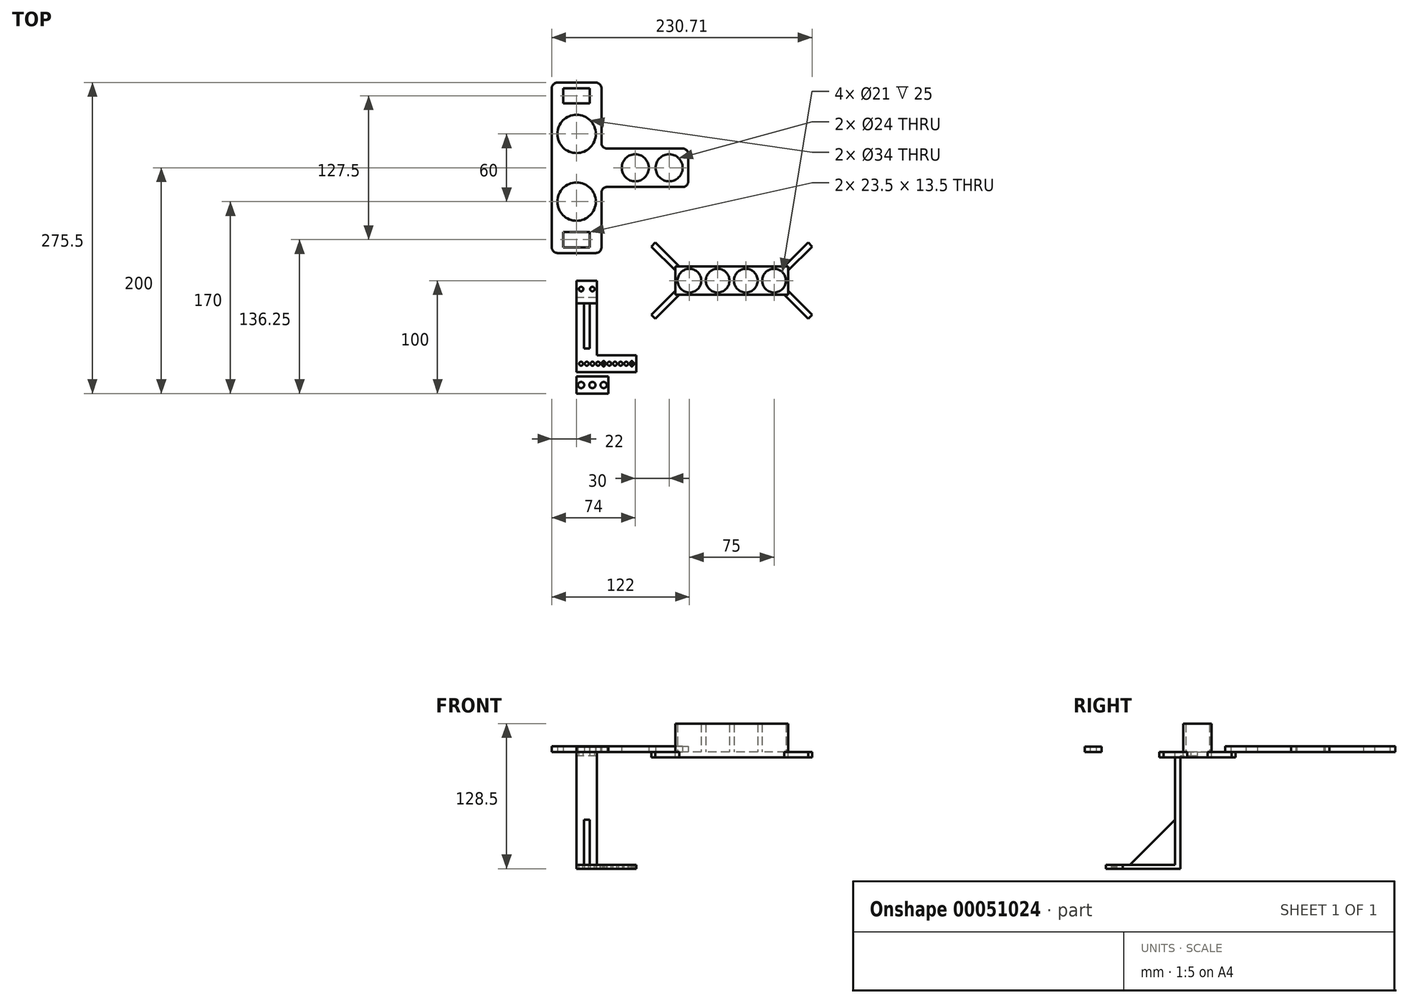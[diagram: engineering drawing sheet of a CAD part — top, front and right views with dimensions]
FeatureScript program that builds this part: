
annotation { "Feature Type Name" : "Feature", "Feature Type Description" : "" }
export const myFeature = defineFeature(function(context is Context, id is Id, definition is map)
    precondition{}
    {
        {
            var Q0;
            Q0=qCreatedBy(makeId("Top.planeOp"),FACE);
            var sketch = newSketch(context, id + "F0", { "sketchPlane" : qUnion([Q0])});
            skLineSegment(sketch, "E0", {"start": v(-42.25, 0) * mm, "end": v(184.17, 0) * mm, "construction": true});
            skCircle(sketch, "E1", {"center": v(0, 30) * mm, "radius": 17 * mm});
            skLineSegment(sketch, "E2.direction1", {"start": v(0, 30) * mm, "end": v(0, -25) * mm, "construction": true});
            skLineSegment(sketch, "E3", {"start": v(-80.48, 30) * mm, "end": v(147.23, 30) * mm, "construction": true});
            skCircle(sketch, "E4.MirrorC", {"center": v(0, -30) * mm, "radius": 17 * mm});
            skLineSegment(sketch, "E5.bottom", {"start": v(-11.75, 70.5) * mm, "end": v(11.75, 70.5) * mm});
            skLineSegment(sketch, "E5.top", {"start": v(-11.75, 57) * mm, "end": v(11.75, 57) * mm});
            skLineSegment(sketch, "E5.left", {"start": v(-11.75, 70.5) * mm, "end": v(-11.75, 57) * mm});
            skLineSegment(sketch, "E5.right", {"start": v(11.75, 70.5) * mm, "end": v(11.75, 57) * mm});
            skLineSegment(sketch, "E6.MirrorCS", {"start": v(-11.75, -57) * mm, "end": v(11.75, -57) * mm});
            skLineSegment(sketch, "E7.MirrorCS", {"start": v(-11.75, -70.5) * mm, "end": v(-11.75, -57) * mm});
            skLineSegment(sketch, "E8.MirrorCS", {"start": v(11.75, -70.5) * mm, "end": v(11.75, -57) * mm});
            skLineSegment(sketch, "E9.MirrorCS", {"start": v(-11.75, -70.5) * mm, "end": v(11.75, -70.5) * mm});
            skLineSegment(sketch, "E10", {"start": v(-22, 0) * mm, "end": v(-22, 75.5) * mm});
            skLineSegment(sketch, "E11", {"start": v(-22, 75.5) * mm, "end": v(22, 75.5) * mm});
            skLineSegment(sketch, "E12", {"start": v(22, 75.5) * mm, "end": v(22, 17) * mm});
            skLineSegment(sketch, "E13", {"start": v(22, 17) * mm, "end": v(99, 17) * mm});
            skLineSegment(sketch, "E14", {"start": v(99, 17) * mm, "end": v(99, 0) * mm});
            skLineSegment(sketch, "E15.MirrorCS", {"start": v(99, -17) * mm, "end": v(99, 0) * mm});
            skLineSegment(sketch, "E16.MirrorCS", {"start": v(22, -17) * mm, "end": v(99, -17) * mm});
            skLineSegment(sketch, "E17.MirrorCS", {"start": v(22, -75.5) * mm, "end": v(22, -17) * mm});
            skLineSegment(sketch, "E18.MirrorCS", {"start": v(-22, 0) * mm, "end": v(-22, -75.5) * mm});
            skLineSegment(sketch, "E19.MirrorCS", {"start": v(-22, -75.5) * mm, "end": v(22, -75.5) * mm});
            skCircle(sketch, "E20", {"center": v(82, 0) * mm, "radius": 12 * mm});
            skCircle(sketch, "E21", {"center": v(52, 0) * mm, "radius": 12 * mm});
            skSolve(sketch);
        }
        {
            var Q0;
            Q0 = qSketchRegion(id + "F0", true);
            extrude(context, id + "F1", {"entities" : qUnion([Q0]), "depth" : 5 * mm});
        }
        {
            var Q0;
            Q0=makeQuery(id+"F1.opExtrude","SWEPT_EDGE",EDGE,{"disambiguationData":[OSD([sQuery(id+"F0.wireOp",EDGE,"E12"),sQuery(id+"F0.wireOp",EDGE,"E13")])]});
            var Q1;
            Q1=makeQuery(id+"F1.opExtrude","SWEPT_EDGE",EDGE,{"disambiguationData":[OSD([sQuery(id+"F0.wireOp",EDGE,"E16.MirrorCS"),sQuery(id+"F0.wireOp",EDGE,"E17.MirrorCS")])]});
            var Q2;
            Q2=makeQuery(id+"F1.opExtrude","SWEPT_EDGE",EDGE,{"disambiguationData":[OSD([sQuery(id+"F0.wireOp",EDGE,"E15.MirrorCS"),sQuery(id+"F0.wireOp",EDGE,"E16.MirrorCS")])]});
            var Q3;
            Q3=makeQuery(id+"F1.opExtrude","SWEPT_EDGE",EDGE,{"disambiguationData":[OSD([sQuery(id+"F0.wireOp",EDGE,"E13"),sQuery(id+"F0.wireOp",EDGE,"E14")])]});
            var Q4;
            Q4=makeQuery(id+"F1.opExtrude","SWEPT_EDGE",EDGE,{"disambiguationData":[OSD([sQuery(id+"F0.wireOp",EDGE,"E11"),sQuery(id+"F0.wireOp",EDGE,"E12")])]});
            var Q5;
            Q5=makeQuery(id+"F1.opExtrude","SWEPT_EDGE",EDGE,{"disambiguationData":[OSD([sQuery(id+"F0.wireOp",EDGE,"E10"),sQuery(id+"F0.wireOp",EDGE,"E11")])]});
            var Q6;
            Q6=makeQuery(id+"F1.opExtrude","SWEPT_EDGE",EDGE,{"disambiguationData":[OSD([sQuery(id+"F0.wireOp",EDGE,"E18.MirrorCS"),sQuery(id+"F0.wireOp",EDGE,"E19.MirrorCS")])]});
            var Q7;
            Q7=makeQuery(id+"F1.opExtrude","SWEPT_EDGE",EDGE,{"disambiguationData":[OSD([sQuery(id+"F0.wireOp",EDGE,"E17.MirrorCS"),sQuery(id+"F0.wireOp",EDGE,"E19.MirrorCS")])]});
            fillet(context, id + "F2", {"entities" : qUnion([Q0, Q1, Q2, Q3, Q4, Q5, Q6, Q7]), "radius" : 5 * mm, "tangentPropagation" : true, "allowEdgeOverflow" : false});
        }
        {
            var Q0;
            Q0=makeQuery(id+"F1.opExtrude","SWEPT_BODY",BODY,{"disambiguationData":[OSD([sQuery(id+"F0.wireOp",EDGE,"E1"),sQuery(id+"F0.wireOp",EDGE,"7cc51740-4756-41ca-b782-dbcf211370ed"),sQuery(id+"F0.wireOp",EDGE,"5a0141ee-e843-40b7-996c-c0bd889232490.MirrorC"),sQuery(id+"F0.wireOp",EDGE,"E4.MirrorC"),sQuery(id+"F0.wireOp",EDGE,"E5.bottom"),sQuery(id+"F0.wireOp",EDGE,"E5.top"),sQuery(id+"F0.wireOp",EDGE,"E5.left"),sQuery(id+"F0.wireOp",EDGE,"E5.right"),sQuery(id+"F0.wireOp",EDGE,"E6.MirrorCS"),sQuery(id+"F0.wireOp",EDGE,"E7.MirrorCS"),sQuery(id+"F0.wireOp",EDGE,"E8.MirrorCS"),sQuery(id+"F0.wireOp",EDGE,"E9.MirrorCS"),sQuery(id+"F0.wireOp",EDGE,"E10"),sQuery(id+"F0.wireOp",EDGE,"E11"),sQuery(id+"F0.wireOp",EDGE,"E12"),sQuery(id+"F0.wireOp",EDGE,"E13"),sQuery(id+"F0.wireOp",EDGE,"E14"),sQuery(id+"F0.wireOp",EDGE,"E15.MirrorCS"),sQuery(id+"F0.wireOp",EDGE,"E16.MirrorCS"),sQuery(id+"F0.wireOp",EDGE,"E17.MirrorCS"),sQuery(id+"F0.wireOp",EDGE,"E18.MirrorCS"),sQuery(id+"F0.wireOp",EDGE,"E19.MirrorCS")])]});
            transform(context, id + "F3", {"entities" : qUnion([Q0]), "transformType" : TransformType.TRANSLATION_3D, "dx" : 0 * mm, "dy" : 200 * mm, "dz" : 0 * mm, "makeCopy" : false});
        }
        {
            var Q0;
            Q0=qCreatedBy(makeId("Right.planeOp"),FACE);
            var sketch = newSketch(context, id + "F4", { "sketchPlane" : qUnion([Q0])});
            skLineSegment(sketch, "E22.bottom", {"start": v(-15, -3.5) * mm, "end": v(0, -3.5) * mm});
            skLineSegment(sketch, "E22.top", {"start": v(-20, 0) * mm, "end": v(0, 0) * mm});
            skLineSegment(sketch, "E22.left", {"start": v(-20, 0) * mm, "end": v(-20, -3.5) * mm});
            skLineSegment(sketch, "E22.right", {"start": v(0, 0) * mm, "end": v(0, -3.5) * mm});
            skLineSegment(sketch, "E23.top", {"start": v(-20, -103.5) * mm, "end": v(-15, -103.5) * mm});
            skLineSegment(sketch, "E23.left", {"start": v(-20, -3.5) * mm, "end": v(-20, -100) * mm});
            skLineSegment(sketch, "E23.right", {"start": v(-15, -3.5) * mm, "end": v(-15, -103.5) * mm});
            skLineSegment(sketch, "E24.bottom", {"start": v(-15, -103.5) * mm, "end": v(-81.1, -103.5) * mm});
            skLineSegment(sketch, "E24.top", {"start": v(-20, -100) * mm, "end": v(-81.1, -100) * mm});
            skLineSegment(sketch, "E24.left", {"start": v(-15, -103.5) * mm, "end": v(-15, -100) * mm});
            skLineSegment(sketch, "E24.right", {"start": v(-81.1, -103.5) * mm, "end": v(-81.1, -100) * mm});
            skLineSegment(sketch, "E25", {"start": v(-73.6, -42.3) * mm, "end": v(-73.6, -123.52) * mm, "construction": true});
            skLineSegment(sketch, "E26", {"start": v(-7.5, 36.53) * mm, "end": v(-7.5, -125.68) * mm, "construction": true});
            skSolve(sketch);
        }
        {
            var Q0;
            Q0 = qSketchRegion(id + "F4", true);
            extrude(context, id + "F5", {"entities" : qUnion([Q0]), "depth" : 53 * mm});
        }
        {
            var Q0;
            Q0=makeQuery(id+"F5.opExtrude","SWEPT_FACE",FACE,{"disambiguationData":[OSD([sQuery(id+"F4.wireOp",EDGE,"E22.top")])]});
            var sketch = newSketch(context, id + "F6", { "sketchPlane" : qUnion([Q0])});
            skCircle(sketch, "E27", {"center": v(4, -7.5) * mm, "radius": 2 * mm});
            skLineSegment(sketch, "E28", {"start": v(-26.36, -7.5) * mm, "end": v(67.35, -7.5) * mm, "construction": true});
            skCircle(sketch, "E29.1.0.0", {"center": v(14, -7.5) * mm, "radius": 2 * mm});
            skLineSegment(sketch, "E29.direction1", {"start": v(4, -7.5) * mm, "end": v(14, -7.5) * mm, "construction": true});
            skSolve(sketch);
        }
        {
            var Q0;
            Q0 = qSketchRegion(id + "F6", true);
            var Q1;
            Q1=makeQuery(id+"F5.opExtrude","SWEPT_FACE",FACE,{"disambiguationData":[OSD([sQuery(id+"F4.wireOp",EDGE,"E22.bottom")])]});
            extrude(context, id + "F7", {"entities" : qUnion([Q0]), "operationType" : NewBodyOperationType.REMOVE, "endBound" : BoundingType.UP_TO_SURFACE, "oppositeDirection" : true, "endBoundEntityFace" : qUnion([Q1]), "depth" : 25 * mm});
        }
        {
            var Q0;
            Q0=makeQuery(id+"F5.opExtrude","SWEPT_FACE",FACE,{"disambiguationData":[OSD([sQuery(id+"F4.wireOp",EDGE,"E22.top")])]});
            var sketch = newSketch(context, id + "F8", { "sketchPlane" : qUnion([Q0])});
            skLineSegment(sketch, "E30.bottom", {"start": v(53, 0) * mm, "end": v(18, 0) * mm});
            skLineSegment(sketch, "E30.top", {"start": v(53, -66.1) * mm, "end": v(18, -66.1) * mm});
            skLineSegment(sketch, "E30.left", {"start": v(53, 0) * mm, "end": v(53, -66.1) * mm});
            skLineSegment(sketch, "E30.right", {"start": v(18, 0) * mm, "end": v(18, -66.1) * mm});
            skSolve(sketch);
        }
        {
            var Q0;
            Q0 = qSketchRegion(id + "F8", true);
            extrude(context, id + "F9", {"entities" : qUnion([Q0]), "operationType" : NewBodyOperationType.REMOVE, "endBound" : BoundingType.THROUGH_ALL, "oppositeDirection" : true, "depth" : 25 * mm});
        }
        {
            var Q0;
            Q0=makeQuery(id+"F5.opExtrude","SWEPT_FACE",FACE,{"disambiguationData":[OSD([sQuery(id+"F4.wireOp",EDGE,"E24.top")])]});
            var sketch = newSketch(context, id + "F10", { "sketchPlane" : qUnion([Q0])});
            skLineSegment(sketch, "E31", {"start": v(-30.18, -73.6) * mm, "end": v(42.32, -73.6) * mm, "construction": true});
            skCircle(sketch, "E32", {"center": v(4, -73.6) * mm, "radius": 1.75 * mm});
            skCircle(sketch, "E33.1.0.0", {"center": v(9, -73.6) * mm, "radius": 1.75 * mm});
            skCircle(sketch, "E33.2.0.0", {"center": v(14, -73.6) * mm, "radius": 1.75 * mm});
            skLineSegment(sketch, "E33.direction1", {"start": v(4, -73.6) * mm, "end": v(9, -73.6) * mm, "construction": true});
            skCircle(sketch, "E34", {"center": v(24, -75.1) * mm, "radius": 0.9 * mm});
            skCircle(sketch, "E35", {"center": v(24, -73.6) * mm, "radius": 1.5 * mm, "construction": true});
            skCircle(sketch, "E36.1.0", {"center": v(25.5, -73.6) * mm, "radius": 0.9 * mm});
            skLineSegment(sketch, "E36.1.1", {"start": v(24, -127.78) * mm, "end": v(24, -55.28) * mm, "construction": true});
            skCircle(sketch, "E36.2.0", {"center": v(24, -72.1) * mm, "radius": 0.9 * mm});
            skLineSegment(sketch, "E36.2.1", {"start": v(78.18, -73.6) * mm, "end": v(5.68, -73.6) * mm, "construction": true});
            skCircle(sketch, "E36.3.0", {"center": v(22.5, -73.6) * mm, "radius": 0.9 * mm});
            skLineSegment(sketch, "E36.3.1", {"start": v(24, -19.42) * mm, "end": v(24, -91.92) * mm, "construction": true});
            skCircle(sketch, "E37.0.3.0", {"center": v(19, -73.6) * mm, "radius": 1.75 * mm});
            skPoint(sketch, "E38.1.0.0", {"position": v(49, -73.6) * mm});
            skCircle(sketch, "E38.1.0.1", {"center": v(39, -73.6) * mm, "radius": 1.75 * mm});
            skCircle(sketch, "E38.1.0.2", {"center": v(34, -73.6) * mm, "radius": 1.75 * mm});
            skCircle(sketch, "E38.1.0.3", {"center": v(29, -73.6) * mm, "radius": 1.75 * mm});
            skCircle(sketch, "E38.1.0.4", {"center": v(44, -73.6) * mm, "radius": 1.75 * mm});
            skCircle(sketch, "E38.1.0.5", {"center": v(47.5, -73.6) * mm, "radius": 0.9 * mm});
            skCircle(sketch, "E38.1.0.6", {"center": v(49, -72.1) * mm, "radius": 0.9 * mm});
            skCircle(sketch, "E38.1.0.7", {"center": v(50.5, -73.6) * mm, "radius": 0.9 * mm});
            skCircle(sketch, "E38.1.0.8", {"center": v(49, -73.6) * mm, "radius": 1.5 * mm, "construction": true});
            skCircle(sketch, "E38.1.0.9", {"center": v(49, -75.1) * mm, "radius": 0.9 * mm});
            skLineSegment(sketch, "E38.1.0.10", {"start": v(29, -73.6) * mm, "end": v(34, -73.6) * mm, "construction": true});
            skLineSegment(sketch, "E38.direction1", {"start": v(24, -73.6) * mm, "end": v(49, -73.6) * mm, "construction": true});
            skSolve(sketch);
        }
        {
            var Q0;
            Q0 = qSketchRegion(id + "F10", true);
            extrude(context, id + "F11", {"entities" : qUnion([Q0]), "operationType" : NewBodyOperationType.REMOVE, "endBound" : BoundingType.UP_TO_NEXT, "oppositeDirection" : true, "depth" : 25 * mm});
        }
        {
            var Q0;
            Q0=qCreatedBy(makeId("Right.planeOp"),FACE);
            cPlane(context, id + "F12", {"entities" : qUnion([Q0]), "cplaneType" : CPlaneType.OFFSET, "offset" : 9 * mm, "width" : 150 * mm, "height" : 150 * mm});
        }
        {
            var Q0;
            Q0=qCreatedBy(id+"F12.planeOp",FACE);
            var sketch = newSketch(context, id + "F13", { "sketchPlane" : qUnion([Q0])});
            skLineSegment(sketch, "E39", {"start": v(-20, -100) * mm, "end": v(-60, -100) * mm});
            skLineSegment(sketch, "E40", {"start": v(-60, -100) * mm, "end": v(-20, -60) * mm});
            skLineSegment(sketch, "E41", {"start": v(-20, -60) * mm, "end": v(-20, -100) * mm});
            skSolve(sketch);
        }
        {
            var Q0;
            Q0 = qSketchRegion(id + "F13", true);
            extrude(context, id + "F14", {"entities" : qUnion([Q0]), "operationType" : NewBodyOperationType.ADD, "endBound" : BoundingType.SYMMETRIC, "depth" : 5 * mm, "hasSecondDirection" : true, "secondDirectionOppositeDirection" : true, "secondDirectionDepth" : 2.5 * mm});
        }
        {
            var Q0;
            Q0=makeQuery(id+"F5.opExtrude","SWEPT_BODY",BODY,{"disambiguationData":[OSD([sQuery(id+"F4.wireOp",EDGE,"E22.bottom"),sQuery(id+"F4.wireOp",EDGE,"E22.top"),sQuery(id+"F4.wireOp",EDGE,"E22.left"),sQuery(id+"F4.wireOp",EDGE,"E22.right"),sQuery(id+"F4.wireOp",EDGE,"E23.left"),sQuery(id+"F4.wireOp",EDGE,"E23.right"),sQuery(id+"F4.wireOp",EDGE,"E24.bottom"),sQuery(id+"F4.wireOp",EDGE,"E24.top"),sQuery(id+"F4.wireOp",EDGE,"E24.left"),sQuery(id+"F4.wireOp",EDGE,"E24.right")])]});
            transform(context, id + "F15", {"entities" : qUnion([Q0]), "transformType" : TransformType.TRANSLATION_3D, "dx" : 0 * mm, "dy" : 100 * mm, "dz" : 0 * mm, "makeCopy" : false});
        }
        {
            var Q0;
            Q0=qCreatedBy(makeId("Top.planeOp"),FACE);
            var sketch = newSketch(context, id + "F16", { "sketchPlane" : qUnion([Q0])});
            skCircle(sketch, "E42", {"center": v(0, 0) * mm, "radius": 10.5 * mm});
            skCircle(sketch, "E43.1.0.0", {"center": v(25, 0) * mm, "radius": 10.5 * mm});
            skCircle(sketch, "E43.2.0.0", {"center": v(50, 0) * mm, "radius": 10.5 * mm});
            skCircle(sketch, "E43.3.0.0", {"center": v(75, 0) * mm, "radius": 10.5 * mm});
            skLineSegment(sketch, "E43.direction1", {"start": v(0, 0) * mm, "end": v(25, 0) * mm, "construction": true});
            skLineSegment(sketch, "E44.bottom", {"start": v(-12.5, 12.5) * mm, "end": v(87.5, 12.5) * mm});
            skLineSegment(sketch, "E44.top", {"start": v(-12.5, -12.5) * mm, "end": v(87.5, -12.5) * mm});
            skLineSegment(sketch, "E44.left", {"start": v(-12.5, 12.5) * mm, "end": v(-12.5, -12.5) * mm});
            skLineSegment(sketch, "E44.right", {"start": v(87.5, 12.5) * mm, "end": v(87.5, -12.5) * mm});
            skSolve(sketch);
        }
        {
            var Q0;
            Q0 = qSketchRegion(id + "F16", true);
            extrude(context, id + "F17", {"entities" : qUnion([Q0]), "depth" : 25 * mm});
        }
        {
            var Q0;
            Q0=makeQuery(id+"F17.opExtrude","CAP_FACE",FACE,{"disambiguationData":[OSD([sQuery(id+"F16.wireOp",EDGE,"E42"),sQuery(id+"F16.wireOp",EDGE,"E43.1.0.0"),sQuery(id+"F16.wireOp",EDGE,"E43.2.0.0"),sQuery(id+"F16.wireOp",EDGE,"E43.3.0.0"),sQuery(id+"F16.wireOp",EDGE,"E44.bottom"),sQuery(id+"F16.wireOp",EDGE,"E44.top"),sQuery(id+"F16.wireOp",EDGE,"E44.left"),sQuery(id+"F16.wireOp",EDGE,"E44.right")])],"isStart":true});
            var sketch = newSketch(context, id + "F18", { "sketchPlane" : qUnion([Q0])});
            skLineSegment(sketch, "E45", {"start": v(-12.5, 0) * mm, "end": v(-12.5, 8.96) * mm});
            skLineSegment(sketch, "E46", {"start": v(-8.96, 12.5) * mm, "end": v(37.5, 12.5) * mm});
            skLineSegment(sketch, "E47", {"start": v(37.5, 41.65) * mm, "end": v(37.5, -31.11) * mm, "construction": true});
            skLineSegment(sketch, "E48", {"start": v(-48.83, 0) * mm, "end": v(106.74, 0) * mm, "construction": true});
            skLineSegment(sketch, "E49", {"start": v(-12.5, 8.96) * mm, "end": v(-33.71, 30.18) * mm});
            skLineSegment(sketch, "E50", {"start": v(-33.71, 30.18) * mm, "end": v(-30.18, 33.71) * mm});
            skLineSegment(sketch, "E51", {"start": v(-30.18, 33.71) * mm, "end": v(-8.96, 12.5) * mm});
            skLineSegment(sketch, "E52", {"start": v(0, 0) * mm, "end": v(-44.63, 44.63) * mm, "construction": true});
            skLineSegment(sketch, "E53", {"start": v(-27.38, -5.91) * mm, "end": v(-4.16, 17.3) * mm, "construction": true});
            skLineSegment(sketch, "E54.MirrorCS", {"start": v(108.71, 30.18) * mm, "end": v(105.18, 33.71) * mm});
            skLineSegment(sketch, "E55.MirrorCS", {"start": v(105.18, 33.71) * mm, "end": v(83.96, 12.5) * mm});
            skLineSegment(sketch, "E56.MirrorCS", {"start": v(87.5, 8.96) * mm, "end": v(108.71, 30.18) * mm});
            skLineSegment(sketch, "E57.MirrorCS", {"start": v(87.5, 0) * mm, "end": v(87.5, 8.96) * mm});
            skLineSegment(sketch, "E58.MirrorCS", {"start": v(83.96, 12.5) * mm, "end": v(37.5, 12.5) * mm});
            skLineSegment(sketch, "E59.MirrorCS", {"start": v(-33.71, -30.18) * mm, "end": v(-30.18, -33.71) * mm});
            skLineSegment(sketch, "E60.MirrorCS", {"start": v(87.5, 0) * mm, "end": v(87.5, -8.96) * mm});
            skLineSegment(sketch, "E61.MirrorCS", {"start": v(87.5, -8.96) * mm, "end": v(108.71, -30.18) * mm});
            skLineSegment(sketch, "E62.MirrorCS", {"start": v(105.18, -33.71) * mm, "end": v(83.96, -12.5) * mm});
            skLineSegment(sketch, "E63.MirrorCS", {"start": v(108.71, -30.18) * mm, "end": v(105.18, -33.71) * mm});
            skLineSegment(sketch, "E64.MirrorCS", {"start": v(83.96, -12.5) * mm, "end": v(37.5, -12.5) * mm});
            skLineSegment(sketch, "E65.MirrorCS", {"start": v(-12.5, 0) * mm, "end": v(-12.5, -8.96) * mm});
            skLineSegment(sketch, "E66.MirrorCS", {"start": v(-8.96, -12.5) * mm, "end": v(37.5, -12.5) * mm});
            skLineSegment(sketch, "E67.MirrorCS", {"start": v(-30.18, -33.71) * mm, "end": v(-8.96, -12.5) * mm});
            skLineSegment(sketch, "E68.MirrorCS", {"start": v(-12.5, -8.96) * mm, "end": v(-33.71, -30.18) * mm});
            skSolve(sketch);
        }
        {
            var Q0;
            Q0 = qSketchRegion(id + "F18", true);
            extrude(context, id + "F19", {"entities" : qUnion([Q0]), "operationType" : NewBodyOperationType.ADD, "depth" : 5 * mm});
        }
        {
            var Q0;
            Q0=makeQuery(id+"F17.opExtrude","SWEPT_BODY",BODY,{"disambiguationData":[OSD([sQuery(id+"F16.wireOp",EDGE,"E42"),sQuery(id+"F16.wireOp",EDGE,"E43.1.0.0"),sQuery(id+"F16.wireOp",EDGE,"E43.2.0.0"),sQuery(id+"F16.wireOp",EDGE,"E43.3.0.0"),sQuery(id+"F16.wireOp",EDGE,"E44.bottom"),sQuery(id+"F16.wireOp",EDGE,"E44.top"),sQuery(id+"F16.wireOp",EDGE,"E44.left"),sQuery(id+"F16.wireOp",EDGE,"E44.right")])]});
            transform(context, id + "F20", {"entities" : qUnion([Q0]), "transformType" : TransformType.TRANSLATION_3D, "dx" : 100 * mm, "dy" : 100 * mm, "dz" : 0 * mm, "makeCopy" : false});
        }
        {
            var Q0;
            Q0=qCreatedBy(makeId("Top.planeOp"),FACE);
            var sketch = newSketch(context, id + "F21", { "sketchPlane" : qUnion([Q0])});
            skLineSegment(sketch, "E69.bottom", {"start": v(0, 15) * mm, "end": v(28, 15) * mm});
            skLineSegment(sketch, "E69.top", {"start": v(0, 0) * mm, "end": v(28, 0) * mm});
            skLineSegment(sketch, "E69.left", {"start": v(0, 15) * mm, "end": v(0, 0) * mm});
            skLineSegment(sketch, "E69.right", {"start": v(28, 15) * mm, "end": v(28, 0) * mm});
            skLineSegment(sketch, "E70", {"start": v(-47.59, 7.5) * mm, "end": v(71.2, 7.5) * mm, "construction": true});
            skLineSegment(sketch, "E71", {"start": v(14, 22.1) * mm, "end": v(14, -42.69) * mm, "construction": true});
            skCircle(sketch, "E72", {"center": v(4, 7.5) * mm, "radius": 2.75 * mm});
            skCircle(sketch, "E73.1.0.0", {"center": v(14, 7.5) * mm, "radius": 2.75 * mm});
            skCircle(sketch, "E73.2.0.0", {"center": v(24, 7.5) * mm, "radius": 2.75 * mm});
            skLineSegment(sketch, "E73.direction1", {"start": v(4, 7.5) * mm, "end": v(14, 7.5) * mm, "construction": true});
            skSolve(sketch);
        }
        {
            var Q0;
            Q0 = qSketchRegion(id + "F21", true);
            extrude(context, id + "F22", {"entities" : qUnion([Q0]), "depth" : 4.5 * mm});
        }
    });
